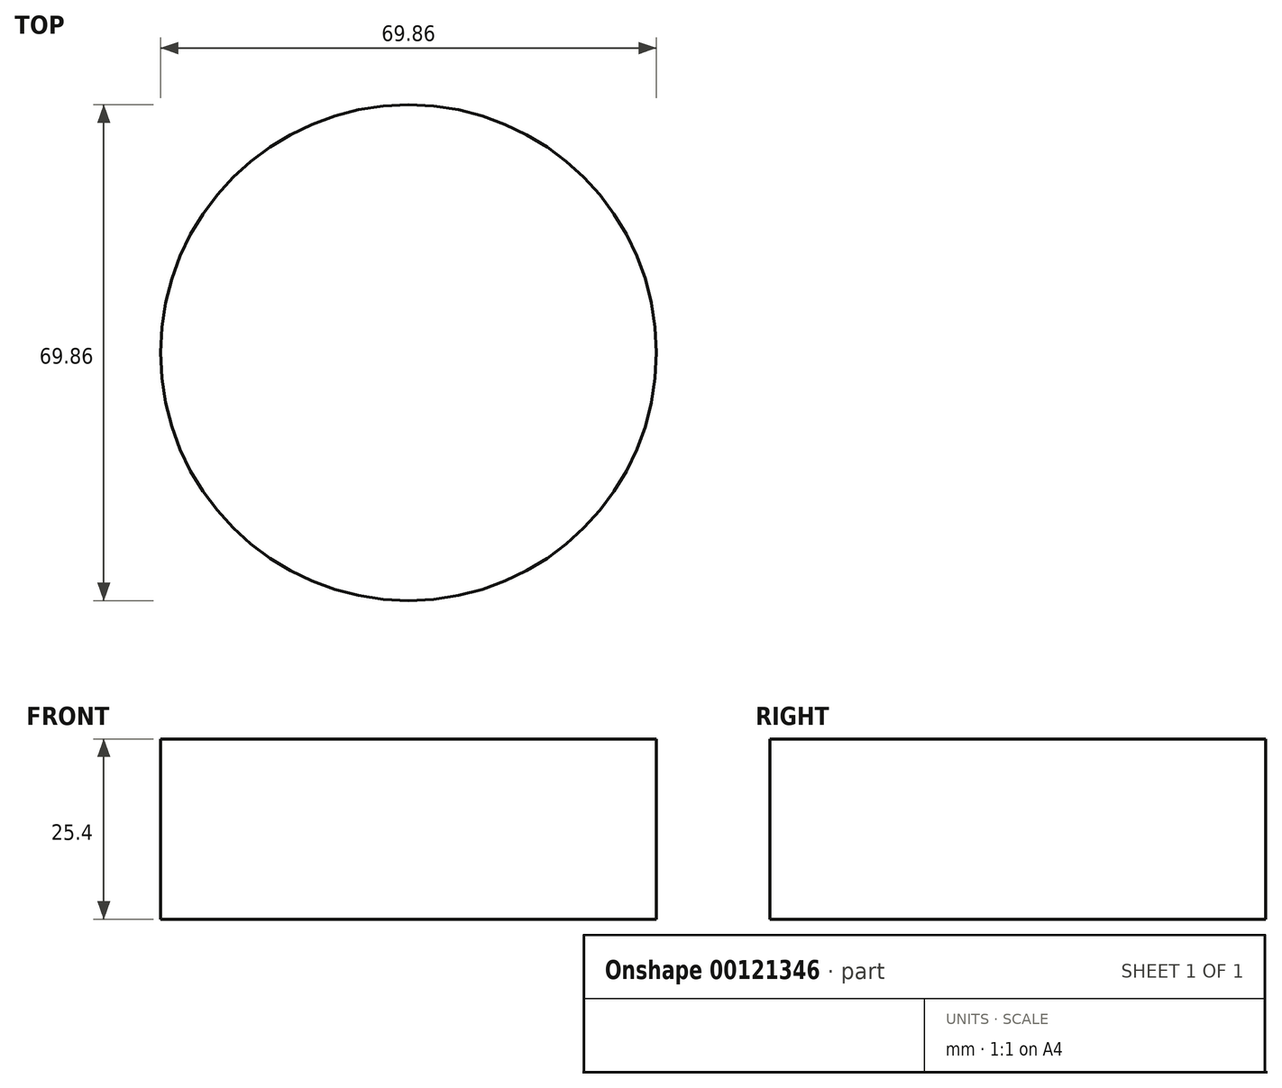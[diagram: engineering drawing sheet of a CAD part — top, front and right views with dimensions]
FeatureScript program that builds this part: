
annotation { "Feature Type Name" : "Feature", "Feature Type Description" : "" }
export const myFeature = defineFeature(function(context is Context, id is Id, definition is map)
    precondition{}
    {
        {
            var Q0;
            Q0=qCreatedBy(makeId("Top.planeOp"),FACE);
            var sketch = newSketch(context, id + "F0", { "sketchPlane" : qUnion([Q0])});
            skCircle(sketch, "E0", {"center": v(0, 0) * mm, "radius": 34.93 * mm});
            skSolve(sketch);
        }
        {
            var Q0;
            Q0 = qSketchRegion(id + "F0", true);
            var Q1;
            Q1=sQuery(id+"F0.wireOp",EDGE,"E0");
            extrude(context, id + "F1", {"entities" : qUnion([Q0]), "bodyType" : ToolBodyType.SURFACE, "surfaceEntities" : qUnion([Q1]), "depth" : 25.4 * mm});
        }
    });
